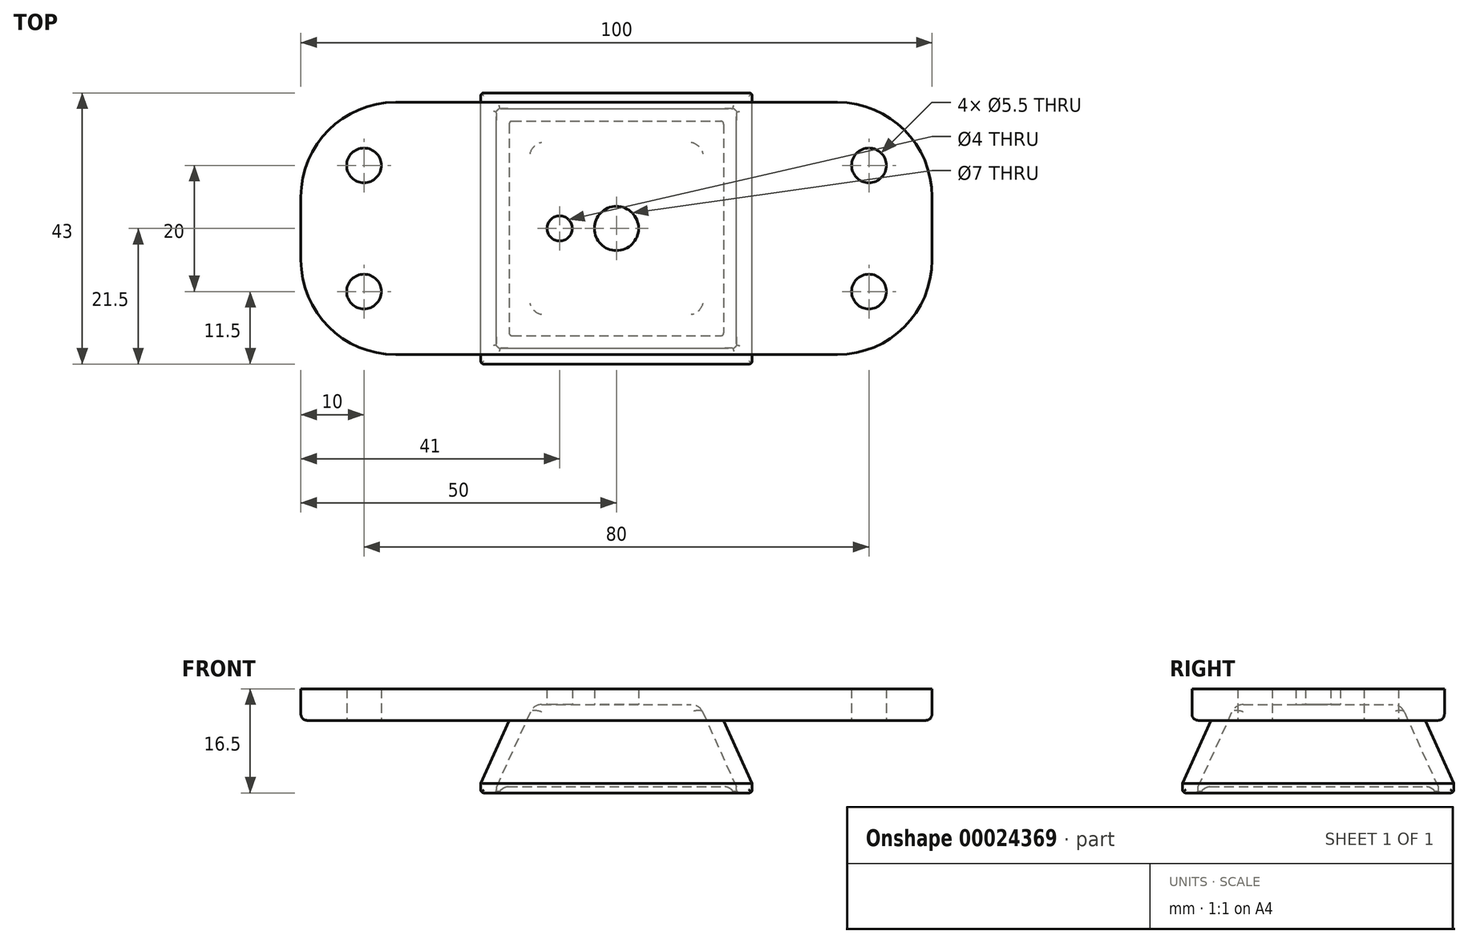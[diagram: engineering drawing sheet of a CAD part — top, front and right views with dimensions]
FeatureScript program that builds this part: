
annotation { "Feature Type Name" : "Feature", "Feature Type Description" : "" }
export const myFeature = defineFeature(function(context is Context, id is Id, definition is map)
    precondition{}
    {
        {
            var Q0;
            Q0=qCreatedBy(makeId("Top.planeOp"),FACE);
            var sketch = newSketch(context, id + "F0", { "sketchPlane" : qUnion([Q0])});
            skLineSegment(sketch, "E0.bottom", {"start": v(-21.5, -21.5) * mm, "end": v(21.5, -21.5) * mm});
            skLineSegment(sketch, "E0.top", {"start": v(-21.5, 21.5) * mm, "end": v(21.5, 21.5) * mm});
            skLineSegment(sketch, "E0.left", {"start": v(-21.5, -21.5) * mm, "end": v(-21.5, 21.5) * mm});
            skLineSegment(sketch, "E0.right", {"start": v(21.5, -21.5) * mm, "end": v(21.5, 21.5) * mm});
            skLineSegment(sketch, "E1", {"start": v(0, 21.5) * mm, "end": v(0, -21.5) * mm, "construction": true});
            skLineSegment(sketch, "E2", {"start": v(-21.5, 0) * mm, "end": v(21.5, 0) * mm, "construction": true});
            skSolve(sketch);
        }
        {
            var Q0;
            Q0=makeQuery(id+"F0.imprint","IMPRINT",FACE,{"disambiguationData":[TD([[makeQuery(id+"F0.imprint","IMPRINT",EDGE,{"derivedFrom":sQuery(id+"F0.wireOp",EDGE,"E0.bottom")}),1.0]])]});
            cPlane(context, id + "F1", {"entities" : qUnion([Q0]), "cplaneType" : CPlaneType.OFFSET, "offset" : 10 * mm, "width" : 150 * mm, "height" : 150 * mm});
        }
        {
            var Q0;
            Q0=qCreatedBy(id+"F1.planeOp",FACE);
            var sketch = newSketch(context, id + "F2", { "sketchPlane" : qUnion([Q0])});
            skLineSegment(sketch, "E3.bottom", {"start": v(-17, 17) * mm, "end": v(17, 17) * mm});
            skLineSegment(sketch, "E3.top", {"start": v(-17, -17) * mm, "end": v(17, -17) * mm});
            skLineSegment(sketch, "E3.left", {"start": v(-17, 17) * mm, "end": v(-17, -17) * mm});
            skLineSegment(sketch, "E3.right", {"start": v(17, 17) * mm, "end": v(17, -17) * mm});
            skLineSegment(sketch, "E4", {"start": v(0, 17) * mm, "end": v(0, -17) * mm, "construction": true});
            skLineSegment(sketch, "E5", {"start": v(-17, 0) * mm, "end": v(17, 0) * mm, "construction": true});
            skSolve(sketch);
        }
        {
            var Q0;
            Q0=makeQuery(id+"F0.imprint","IMPRINT",FACE,{"disambiguationData":[TD([[makeQuery(id+"F0.imprint","IMPRINT",EDGE,{"derivedFrom":sQuery(id+"F0.wireOp",EDGE,"E0.bottom")}),1.0]])]});
            var Q1;
            Q1=makeQuery(id+"F2.imprint","IMPRINT",FACE,{"disambiguationData":[TD([[makeQuery(id+"F2.imprint","IMPRINT",EDGE,{"derivedFrom":sQuery(id+"F2.wireOp",EDGE,"E3.bottom")}),-1.0]])]});
            loft(context, id + "F3", {"sheetProfilesArray" : [{ "sheetProfileEntities" : qUnion([Q0]) }, { "sheetProfileEntities" : qUnion([Q1]) }]});
        }
        {
            var Q0;
            Q0=makeQuery(id+"F3.opLoft","CAP_FACE",FACE,{"disambiguationData":[OSD([makeQuery(id+"F2.imprint","IMPRINT",FACE,{"disambiguationData":[TD([[makeQuery(id+"F2.imprint","IMPRINT",EDGE,{"derivedFrom":sQuery(id+"F2.wireOp",EDGE,"E3.bottom")}),-1.0]])]})])],"isStart":true});
            var sketch = newSketch(context, id + "F4", { "sketchPlane" : qUnion([Q0])});
            skLineSegment(sketch, "E6.bottom", {"start": v(-35, 20) * mm, "end": v(35, 20) * mm});
            skLineSegment(sketch, "E6.top", {"start": v(-35, -20) * mm, "end": v(35, -20) * mm});
            skLineSegment(sketch, "E6.left", {"start": v(-50, 5) * mm, "end": v(-50, -5) * mm});
            skLineSegment(sketch, "E6.right", {"start": v(50, 5) * mm, "end": v(50, -5) * mm});
            skLineSegment(sketch, "E7", {"start": v(0, 20) * mm, "end": v(0, 0) * mm, "construction": true});
            skLineSegment(sketch, "E8", {"start": v(0, 0) * mm, "end": v(50, 0) * mm, "construction": true});
            skLineSegment(sketch, "E9", {"start": v(-21.5, 0) * mm, "end": v(-50, 0) * mm, "construction": true});
            skPoint(sketch, "E10.visualSharp", {"position": v(-50, -20) * mm});
            skArc(sketch, "E10.filletArc", {"start": v(-50, -5) * mm, "mid": v(-45.6, -15.6) * mm, "end": v(-35, -20) * mm});
            skPoint(sketch, "E11.visualSharp", {"position": v(-50, 20) * mm});
            skArc(sketch, "E11.filletArc", {"start": v(-35, 20) * mm, "mid": v(-45.6, 15.6) * mm, "end": v(-50, 5) * mm});
            skPoint(sketch, "E12.visualSharp", {"position": v(50, -20) * mm});
            skArc(sketch, "E12.filletArc", {"start": v(35, -20) * mm, "mid": v(45.6, -15.6) * mm, "end": v(50, -5) * mm});
            skPoint(sketch, "E13.visualSharp", {"position": v(50, 20) * mm});
            skArc(sketch, "E13.filletArc", {"start": v(50, 5) * mm, "mid": v(45.6, 15.6) * mm, "end": v(35, 20) * mm});
            skLineSegment(sketch, "E14", {"start": v(-40, 0) * mm, "end": v(-40, 10) * mm, "construction": true});
            skCircle(sketch, "E15", {"center": v(-40, 10) * mm, "radius": 2.75 * mm});
            skCircle(sketch, "E16.0.1.0", {"center": v(-40, -10) * mm, "radius": 2.75 * mm});
            skCircle(sketch, "E16.1.0.0", {"center": v(40, 10) * mm, "radius": 2.75 * mm});
            skCircle(sketch, "E16.1.1.0", {"center": v(40, -10) * mm, "radius": 2.75 * mm});
            skLineSegment(sketch, "E16.direction1", {"start": v(-40, 10) * mm, "end": v(40, 10) * mm, "construction": true});
            skLineSegment(sketch, "E16.direction2", {"start": v(-40, 10) * mm, "end": v(-40, -10) * mm, "construction": true});
            skSolve(sketch);
        }
        {
            var Q0;
            Q0=qSketchRegion(id+"F4",true);
            extrude(context, id + "F5", {"entities" : qUnion([Q0]), "operationType" : NewBodyOperationType.ADD, "depth" : 5 * mm});
        }
        {
            var Q0;
            Q0=qSketchRegion(id+"F0",true);
            extrude(context, id + "F6", {"entities" : qUnion([Q0]), "operationType" : NewBodyOperationType.ADD, "oppositeDirection" : true, "depth" : 1.5 * mm});
        }
        {
            var Q0;
            Q0=makeQuery(id+"F6.opExtrude","CAP_FACE",FACE,{"disambiguationData":[OSD([sQuery(id+"F0.wireOp",EDGE,"E0.bottom"),sQuery(id+"F0.wireOp",EDGE,"E0.top"),sQuery(id+"F0.wireOp",EDGE,"E0.left"),sQuery(id+"F0.wireOp",EDGE,"E0.right")])],"isStart":false});
            shell(context, id + "F7", {"entities" : qUnion([Q0]), "thickness" : 2.5 * mm});
        }
        {
            var Q0;
            Q0=makeQuery(id+"F4.imprint","IMPRINT",FACE,{"disambiguationData":[TD([[makeQuery(id+"F4.imprint","IMPRINT",EDGE,{"derivedFrom":sQuery(id+"F4.wireOp",EDGE,"E6.bottom")}),-1.0]])]});
            var sketch = newSketch(context, id + "F8", { "sketchPlane" : qUnion([Q0])});
            skLineSegment(sketch, "E17", {"start": v(0, 0) * mm, "end": v(-9, 0) * mm, "construction": true});
            skCircle(sketch, "E18", {"center": v(0, 0) * mm, "radius": 3.5 * mm});
            skCircle(sketch, "E19", {"center": v(-9, 0) * mm, "radius": 2 * mm});
            skSolve(sketch);
        }
        {
            var Q0;
            Q0=makeQuery(id+"F7.opShell","OFFSET_EDGE",EDGE,{"disambiguationData":[OSD([sQuery(id+"F0.wireOp",EDGE,"E0.bottom"),sQuery(id+"F0.wireOp",EDGE,"E0.left"),sQuery(id+"F2.wireOp",EDGE,"E3.top"),sQuery(id+"F2.wireOp",EDGE,"E3.left")])]});
            var Q1;
            Q1=makeQuery(id+"F7.opShell","OFFSET_EDGE",EDGE,{"disambiguationData":[OSD([sQuery(id+"F0.wireOp",EDGE,"E0.bottom"),sQuery(id+"F0.wireOp",EDGE,"E0.right"),sQuery(id+"F2.wireOp",EDGE,"E3.top"),sQuery(id+"F2.wireOp",EDGE,"E3.right")])]});
            var Q2;
            Q2=makeQuery(id+"F7.opShell","OFFSET_EDGE",EDGE,{"disambiguationData":[OSD([sQuery(id+"F0.wireOp",EDGE,"E0.top"),sQuery(id+"F0.wireOp",EDGE,"E0.right"),sQuery(id+"F2.wireOp",EDGE,"E3.bottom"),sQuery(id+"F2.wireOp",EDGE,"E3.right")])]});
            var Q3;
            Q3=makeQuery(id+"F7.opShell","OFFSET_EDGE",EDGE,{"disambiguationData":[OSD([sQuery(id+"F0.wireOp",EDGE,"E0.top"),sQuery(id+"F0.wireOp",EDGE,"E0.left"),sQuery(id+"F2.wireOp",EDGE,"E3.bottom"),sQuery(id+"F2.wireOp",EDGE,"E3.left")])]});
            var Q4;
            Q4=makeQuery(id+"F7.opShell","OFFSET_FACE",FACE,{"disambiguationData":[OSD([sQuery(id+"F4.wireOp",EDGE,"E6.bottom"),sQuery(id+"F4.wireOp",EDGE,"E6.top"),sQuery(id+"F4.wireOp",EDGE,"E6.left"),sQuery(id+"F4.wireOp",EDGE,"E6.right"),sQuery(id+"F4.wireOp",EDGE,"2fd4213e-9feb-4e0b-9475-6d61dc8a4de1"),sQuery(id+"F4.wireOp",EDGE,"2afbfed0-2c72-4080-8e1d-2d171298e25c0.MirrorC")])]});
            fillet(context, id + "F9", {"entities" : qUnion([Q0, Q1, Q2, Q3, Q4]), "radius" : 2 * mm, "allowEdgeOverflow" : false});
        }
        {
            var Q0;
            Q0=makeQuery(id+"F6.opExtrude","CAP_FACE",FACE,{"disambiguationData":[OSD([sQuery(id+"F0.wireOp",EDGE,"E0.bottom"),sQuery(id+"F0.wireOp",EDGE,"E0.top"),sQuery(id+"F0.wireOp",EDGE,"E0.left"),sQuery(id+"F0.wireOp",EDGE,"E0.right")])],"isStart":false});
            fillet(context, id + "F10", {"entities" : qUnion([Q0]), "radius" : .5 * mm, "tangentPropagation" : true, "allowEdgeOverflow" : false});
        }
        {
            var Q0;
            Q0=makeQuery(id+"F3.opLoft","SWEPT_EDGE",EDGE,{"disambiguationData":[OSD([sQuery(id+"F0.wireOp",EDGE,"E0.bottom"),sQuery(id+"F0.wireOp",EDGE,"E0.left"),sQuery(id+"F2.wireOp",EDGE,"E3.top"),sQuery(id+"F2.wireOp",EDGE,"E3.left")])]});
            var Q1;
            Q1=makeQuery(id+"F3.opLoft","SWEPT_EDGE",EDGE,{"disambiguationData":[OSD([sQuery(id+"F0.wireOp",EDGE,"E0.top"),sQuery(id+"F0.wireOp",EDGE,"E0.left"),sQuery(id+"F2.wireOp",EDGE,"E3.bottom"),sQuery(id+"F2.wireOp",EDGE,"E3.left")])]});
            var Q2;
            Q2=makeQuery(id+"F3.opLoft","SWEPT_EDGE",EDGE,{"disambiguationData":[OSD([sQuery(id+"F0.wireOp",EDGE,"E0.top"),sQuery(id+"F0.wireOp",EDGE,"E0.right"),sQuery(id+"F2.wireOp",EDGE,"E3.bottom"),sQuery(id+"F2.wireOp",EDGE,"E3.right")])]});
            var Q3;
            Q3=makeQuery(id+"F3.opLoft","SWEPT_EDGE",EDGE,{"disambiguationData":[OSD([sQuery(id+"F0.wireOp",EDGE,"E0.bottom"),sQuery(id+"F0.wireOp",EDGE,"E0.right"),sQuery(id+"F2.wireOp",EDGE,"E3.top"),sQuery(id+"F2.wireOp",EDGE,"E3.right")])]});
            var Q4;
            Q4=makeQuery(id+"F6.opExtrude","SWEPT_EDGE",EDGE,{"disambiguationData":[OSD([sQuery(id+"F0.wireOp",EDGE,"E0.bottom"),sQuery(id+"F0.wireOp",EDGE,"E0.left")])]});
            var Q5;
            Q5=makeQuery(id+"F6.opExtrude","SWEPT_EDGE",EDGE,{"disambiguationData":[OSD([sQuery(id+"F0.wireOp",EDGE,"E0.bottom"),sQuery(id+"F0.wireOp",EDGE,"E0.right")])]});
            var Q6;
            Q6=makeQuery(id+"F6.opExtrude","SWEPT_EDGE",EDGE,{"disambiguationData":[OSD([sQuery(id+"F0.wireOp",EDGE,"E0.top"),sQuery(id+"F0.wireOp",EDGE,"E0.right")])]});
            var Q7;
            Q7=makeQuery(id+"F6.opExtrude","SWEPT_EDGE",EDGE,{"disambiguationData":[OSD([sQuery(id+"F0.wireOp",EDGE,"E0.top"),sQuery(id+"F0.wireOp",EDGE,"E0.left")])]});
            fillet(context, id + "F11", {"entities" : qUnion([Q0, Q1, Q2, Q3, Q4, Q5, Q6, Q7]), "radius" : .5 * mm, "allowEdgeOverflow" : false});
        }
        {
            var Q0;
            Q0=makeQuery(id+"F5.opExtrude","CAP_EDGE",EDGE,{"disambiguationData":[OSD([sQuery(id+"F4.wireOp",EDGE,"E6.right")])],"isStart":true});
            var Q1;
            Q1=makeQuery(id+"F5.opExtrude","CAP_EDGE",EDGE,{"disambiguationData":[OSD([sQuery(id+"F4.wireOp",EDGE,"E6.top")])],"isStart":true});
            var Q2;
            Q2=makeQuery(id+"F5.opExtrude","CAP_EDGE",EDGE,{"disambiguationData":[OSD([sQuery(id+"F4.wireOp",EDGE,"E6.bottom")])],"isStart":true});
            var Q3;
            Q3=makeQuery(id+"F5.opExtrude","CAP_EDGE",EDGE,{"disambiguationData":[OSD([sQuery(id+"F4.wireOp",EDGE,"E6.left")])],"isStart":true});
            var Q4;
            Q4=makeQuery(id+"F5.opExtrude","CAP_EDGE",EDGE,{"disambiguationData":[OSD([sQuery(id+"F4.wireOp",EDGE,"E10.filletArc")])],"isStart":true});
            var Q5;
            Q5=makeQuery(id+"F5.opExtrude","CAP_EDGE",EDGE,{"disambiguationData":[OSD([sQuery(id+"F4.wireOp",EDGE,"E12.filletArc")])],"isStart":true});
            var Q6;
            Q6=makeQuery(id+"F5.opExtrude","CAP_EDGE",EDGE,{"disambiguationData":[OSD([sQuery(id+"F4.wireOp",EDGE,"E13.filletArc")])],"isStart":true});
            var Q7;
            Q7=makeQuery(id+"F5.opExtrude","CAP_EDGE",EDGE,{"disambiguationData":[OSD([sQuery(id+"F4.wireOp",EDGE,"E11.filletArc")])],"isStart":true});
            fillet(context, id + "F12", {"entities" : qUnion([Q0, Q1, Q2, Q3, Q4, Q5, Q6, Q7]), "radius" : 1 * mm, "allowEdgeOverflow" : false});
        }
        {
            var Q0;
            Q0=qSketchRegion(id+"F8",true);
            extrude(context, id + "F13", {"entities" : qUnion([Q0]), "operationType" : NewBodyOperationType.REMOVE, "endBound" : BoundingType.THROUGH_ALL, "depth" : 6 * mm});
        }
    });
